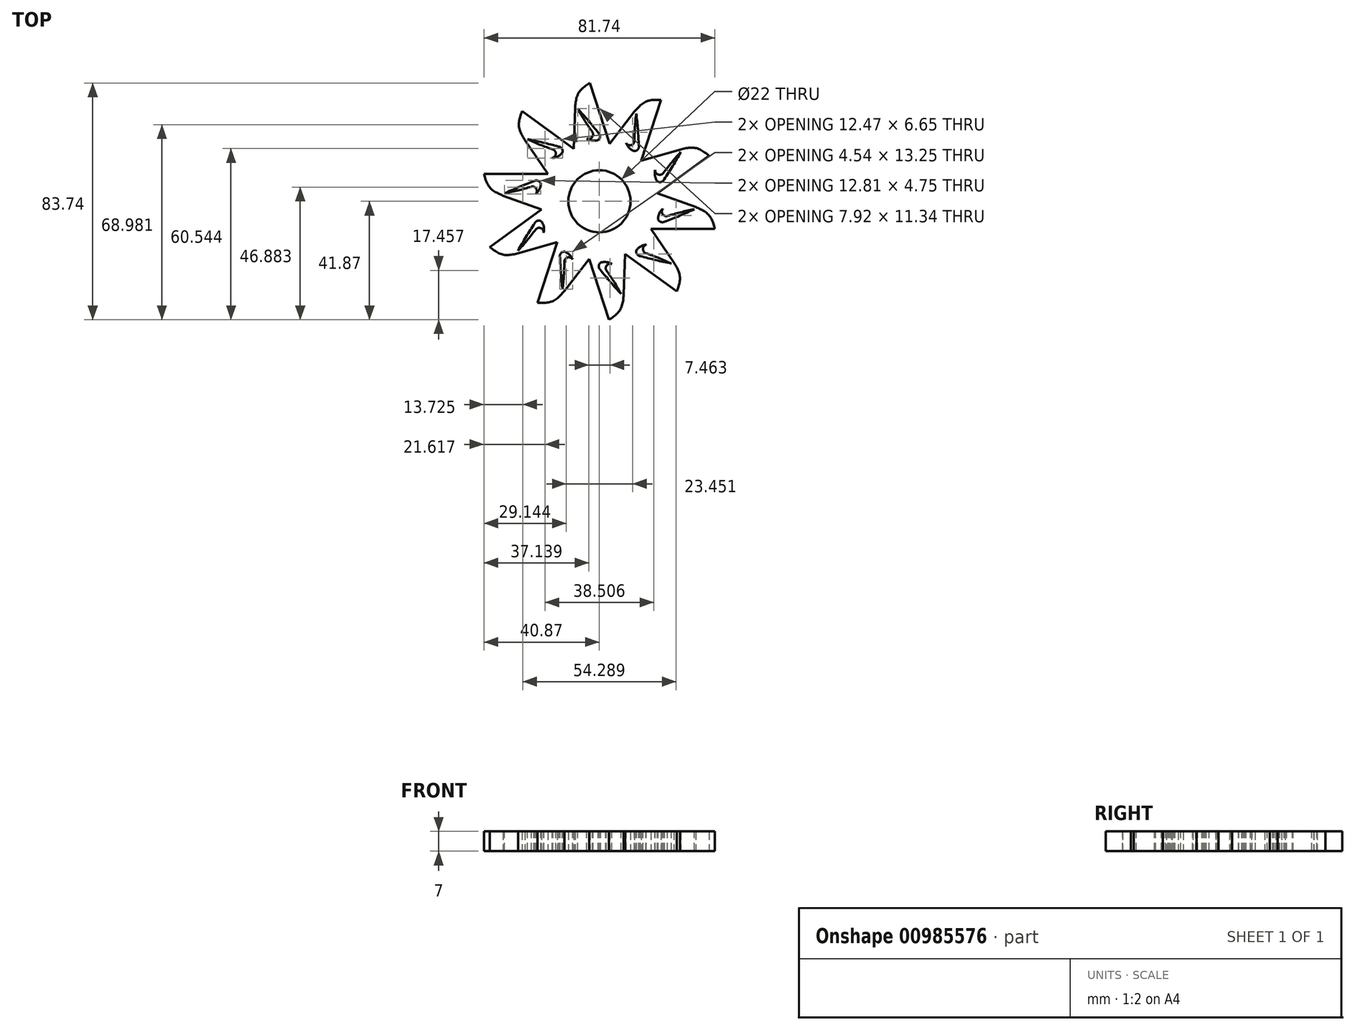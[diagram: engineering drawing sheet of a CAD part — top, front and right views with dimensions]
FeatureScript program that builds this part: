
annotation { "Feature Type Name" : "Feature", "Feature Type Description" : "" }
export const myFeature = defineFeature(function(context is Context, id is Id, definition is map)
    precondition{}
    {
        {
            var Q0;
            Q0=qCreatedBy(makeId("Top.planeOp"),FACE);
            var sketch = newSketch(context, id + "F0", { "sketchPlane" : qUnion([Q0])});
            skCircle(sketch, "E0", {"center": v(0, 0) * mm, "radius": 11 * mm});
            skCircle(sketch, "E1", {"center": v(0, 0) * mm, "radius": 45 * mm, "construction": true});
            skLineSegment(sketch, "E2.bottom", {"start": v(9.29, 5.9) * mm, "end": v(11.3, 5.9) * mm});
            skLineSegment(sketch, "E2.top", {"start": v(5.2, -9.7) * mm, "end": v(40.87, -9.7) * mm});
            skLineSegment(sketch, "E2.right", {"start": v(13, 5.6) * mm, "end": v(34.05, -2) * mm});
            skCircle(sketch, "E3", {"center": v(0, 0) * mm, "radius": 20 * mm});
            skCircle(sketch, "E4", {"center": v(-5.3, -5.3) * mm, "radius": 1 * mm});
            skPoint(sketch, "E5.visualSharp", {"position": v(12.17, 5.9) * mm});
            skArc(sketch, "E5.filletArc", {"start": v(13, 5.6) * mm, "mid": v(12.15, 5.82) * mm, "end": v(11.3, 5.9) * mm});
            skPoint(sketch, "E6.visualSharp", {"position": v(55.33, -9.7) * mm});
            skFitSpline(sketch, "E7", {"points": [v(34.05, -2) * mm, v(38.72, -4.83) * mm, v(40.87, -9.7) * mm], "startDerivative": vector(10.5, -4.57) * mm, "endDerivative": vector(3.12, -10.82) * mm});
            skSolve(sketch);
        }
        {
            var Q0;
            {var subQ8=sQuery(id+"F0.wireOp",EDGE,"E2.bottom");Q0=makeQuery(id+"F0.imprint","IMPRINT",FACE,{"disambiguationData":[TD([[makeQuery(id+"F0.imprint","IMPRINT",EDGE,{"derivedFrom":subQ8}),-1.0]])]});}
            var Q1;
            {var subQ5=sQuery(id+"F0.wireOp",EDGE,"E2.bottom");Q1=makeQuery(id+"F0.imprint","IMPRINT",FACE,{"disambiguationData":[TD([[makeQuery(id+"F0.imprint","IMPRINT",EDGE,{"derivedFrom":subQ5}),1.0]])]});}
            var Q2;
            {var subQ0=sQuery(id+"F0.wireOp",EDGE,"E7");Q2=makeQuery(id+"F0.imprint","IMPRINT",FACE,{"disambiguationData":[TD([[makeQuery(id+"F0.imprint","IMPRINT",EDGE,{"derivedFrom":subQ0}),-1.0]])]});}
            extrude(context, id + "F1", {"entities" : qUnion([Q0, Q1, Q2]), "depth" : 7 * mm, "offsetDistance" : 25 * mm});
        }
        {
            var Q0;
            Q0=qCreatedBy(makeId("Top.planeOp"),FACE);
            var sketch = newSketch(context, id + "F2", { "sketchPlane" : qUnion([Q0])});
            skArc(sketch, "E8", {"start": v(22.48, -2.64) * mm, "mid": v(21.2, -4.26) * mm, "end": v(20.74, -6.27) * mm});
            skArc(sketch, "E9", {"start": v(20.74, -6.27) * mm, "mid": v(21.7, -7.3) * mm, "end": v(23.11, -7.16) * mm});
            skArc(sketch, "E10", {"start": v(23.11, -7.16) * mm, "mid": v(28.38, -5.1) * mm, "end": v(33.55, -2.82) * mm});
            skArc(sketch, "E11", {"start": v(33.55, -2.82) * mm, "mid": v(28.79, -3.86) * mm, "end": v(24.1, -5.2) * mm});
            skArc(sketch, "E12", {"start": v(22.48, -2.64) * mm, "mid": v(22.34, -4.51) * mm, "end": v(24.1, -5.2) * mm});
            skSolve(sketch);
        }
        {
            var Q0;
            Q0=makeQuery(id+"F2.imprint","IMPRINT",FACE,{"disambiguationData":[TD([[makeQuery(id+"F2.imprint","IMPRINT",EDGE,{"derivedFrom":sQuery(id+"F2.wireOp",EDGE,"E8")}),1.0]])]});
            extrude(context, id + "F3", {"entities" : qUnion([Q0]), "operationType" : NewBodyOperationType.REMOVE, "endBound" : BoundingType.THROUGH_ALL, "oppositeDirection" : true, "depth" : 25 * mm, "offsetDistance" : 25 * mm, "hasSecondDirection" : true, "secondDirectionOppositeDirection" : false, "secondDirectionDepth" : 25 * mm});
        }
        {
            var Q0;
            Q0=makeQuery(id+"F1.opExtrude","SWEPT_BODY",BODY,{"disambiguationData":[OSD([sQuery(id+"F0.wireOp",EDGE,"E0"),sQuery(id+"F0.wireOp",EDGE,"E2.bottom"),sQuery(id+"F0.wireOp",EDGE,"E2.top"),sQuery(id+"F0.wireOp",EDGE,"E2.right")])]});
            var Q1;
            Q1=makeQuery(id+"F1.opExtrude","CAP_EDGE",EDGE,{"disambiguationData":[OSD([sQuery(id+"F0.wireOp",EDGE,"E0")])],"isStart":false});
            circularPattern(context, id + "F4", {"operationType" : NewBodyOperationType.ADD, "entities" : qUnion([Q0]), "axis" : qUnion([Q1]), "angle" : 360 * degree, "instanceCount" : 10, "oppositeDirection" : true, "equalSpace" : true});
        }
    });
